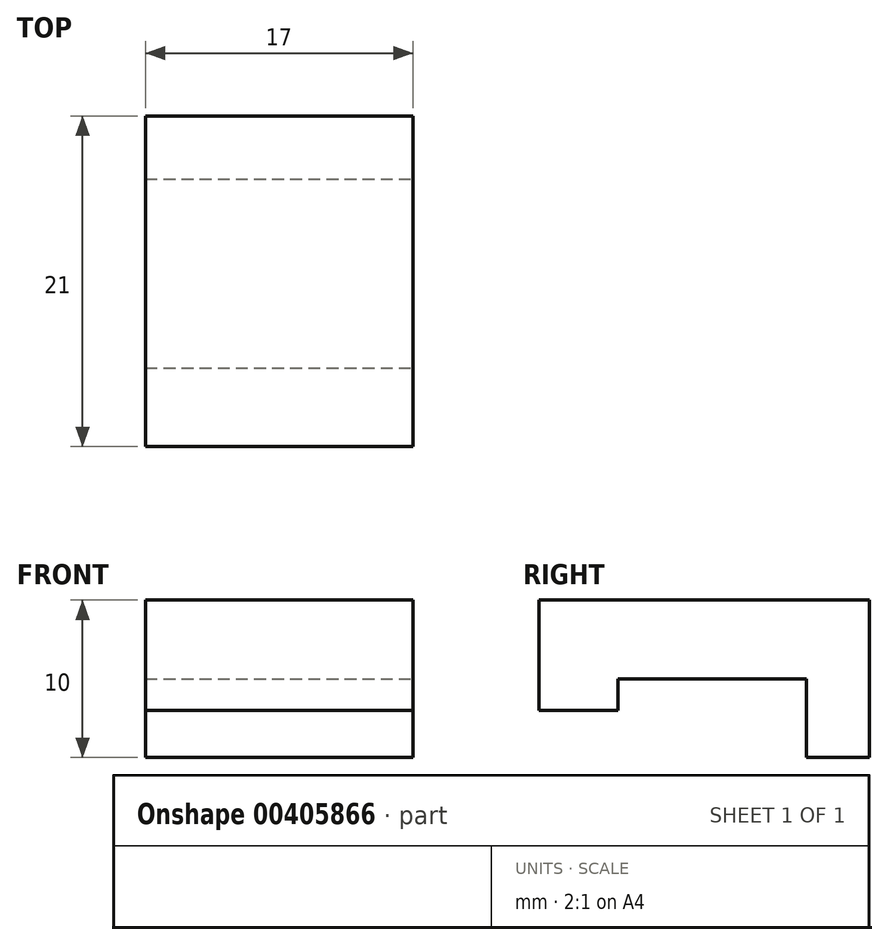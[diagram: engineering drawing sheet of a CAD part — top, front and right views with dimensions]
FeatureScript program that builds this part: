
annotation { "Feature Type Name" : "Feature", "Feature Type Description" : "" }
export const myFeature = defineFeature(function(context is Context, id is Id, definition is map)
    precondition{}
    {
        {
            var Q0;
            Q0=qCreatedBy(makeId("Top.planeOp"),FACE);
            var sketch = newSketch(context, id + "F0", { "sketchPlane" : qUnion([Q0])});
            skLineSegment(sketch, "E0.bottom", {"start": v(-2.98, -4.43) * mm, "end": v(14.02, -4.43) * mm});
            skLineSegment(sketch, "E0.top", {"start": v(-2.98, -8.43) * mm, "end": v(14.02, -8.43) * mm});
            skLineSegment(sketch, "E0.left", {"start": v(-2.98, -4.43) * mm, "end": v(-2.98, -8.43) * mm});
            skLineSegment(sketch, "E0.right", {"start": v(14.02, -4.43) * mm, "end": v(14.02, -8.43) * mm});
            skSolve(sketch);
        }
        {
            var Q0;
            Q0=makeQuery(id+"F0.imprint","IMPRINT",FACE,{"disambiguationData":[TD([[makeQuery(id+"F0.imprint","IMPRINT",EDGE,{"derivedFrom":sQuery(id+"F0.wireOp",EDGE,"E0.bottom")}),-1.0]])]});
            extrude(context, id + "F1", {"entities" : qUnion([Q0]), "depth" : 10 * mm});
        }
        {
            var Q0;
            Q0=makeQuery(id+"F1.opExtrude","SWEPT_FACE",FACE,{"disambiguationData":[OSD([sQuery(id+"F0.wireOp",EDGE,"E0.top")])]});
            var sketch = newSketch(context, id + "F2", { "sketchPlane" : qUnion([Q0])});
            skLineSegment(sketch, "E1.bottom", {"start": v(-2.98, 10) * mm, "end": v(14.02, 10) * mm});
            skLineSegment(sketch, "E1.top", {"start": v(-2.98, 5) * mm, "end": v(14.02, 5) * mm});
            skLineSegment(sketch, "E1.left", {"start": v(-2.98, 10) * mm, "end": v(-2.98, 5) * mm});
            skLineSegment(sketch, "E1.right", {"start": v(14.02, 10) * mm, "end": v(14.02, 5) * mm});
            skSolve(sketch);
        }
        {
            var Q0;
            Q0=makeQuery(id+"F2.imprint","IMPRINT",FACE,{"disambiguationData":[TD([[makeQuery(id+"F2.imprint","IMPRINT",EDGE,{"derivedFrom":sQuery(id+"F2.wireOp",EDGE,"E1.bottom")}),-1.0]])]});
            extrude(context, id + "F3", {"entities" : qUnion([Q0]), "operationType" : NewBodyOperationType.ADD, "depth" : 12 * mm});
        }
        {
            var Q0;
            Q0=makeQuery(id+"F3.opExtrude","CAP_FACE",FACE,{"disambiguationData":[OSD([sQuery(id+"F2.wireOp",EDGE,"E1.bottom"),sQuery(id+"F2.wireOp",EDGE,"E1.top"),sQuery(id+"F2.wireOp",EDGE,"E1.left"),sQuery(id+"F2.wireOp",EDGE,"E1.right")])],"isStart":false});
            var sketch = newSketch(context, id + "F4", { "sketchPlane" : qUnion([Q0])});
            skLineSegment(sketch, "E2.bottom", {"start": v(-2.98, 10) * mm, "end": v(14.02, 10) * mm});
            skLineSegment(sketch, "E2.top", {"start": v(-2.98, 3) * mm, "end": v(14.02, 3) * mm});
            skLineSegment(sketch, "E2.left", {"start": v(-2.98, 10) * mm, "end": v(-2.98, 3) * mm});
            skLineSegment(sketch, "E2.right", {"start": v(14.02, 10) * mm, "end": v(14.02, 3) * mm});
            skSolve(sketch);
        }
        {
            var Q0;
            Q0 = qSketchRegion(id + "F4", true);
            extrude(context, id + "F5", {"entities" : qUnion([Q0]), "operationType" : NewBodyOperationType.ADD, "depth" : 5 * mm});
        }
    });
